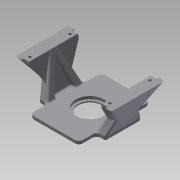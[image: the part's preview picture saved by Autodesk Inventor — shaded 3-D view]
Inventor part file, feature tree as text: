
AUTODESK INVENTOR PART (.ipt)
format: ipt  version: 2015 (Build 190159000, 159)  size: 1,136,128 bytes
history: native  units: in
note: dims shown in document units (in); Inventor stores cm internally (conversion verified against a paired STEP export)
features: fillet x9, sketch x8, extrude x6, plane x3, loft x3, mirror x1
ambient origin geometry x8: Origin, YZ Plane, XZ Plane, XY Plane, X Axis, Y Axis, Z Axis, Center Point
bodies: Solid1 (feature_tree)
feature tree (30):
  extrude  "Extrusion1"  Depth=3.1496in
  extrude  "Extrusion2"  Depth=0.3937in
  plane  "Work Plane1"
  plane  "Work Plane2"
  loft  "Loft3"
  loft  "Loft4"
  fillet  "Fillet1"  Radius=0.1181in
  fillet  "Fillet3"  Radius=1.4961in
  fillet  "Fillet4"  Radius=0.12in
  extrude  "Extrusion6"  Depth=2.126in
  extrude  "Extrusion7"  Depth=0.1772in
  fillet  "Fillet6"  Radius=0.2362in
  loft  "Loft5"
  fillet  "Fillet8"  Radius=0.2362in
  plane  "Work Plane3"
  extrude  "Extrusion8"  Depth=0.1181in
  fillet  "Fillet9"  Radius=2.1654in
  fillet  "Fillet10"  Radius=2.9528in
  fillet  "Fillet11"  Radius=1.5748in
  mirror  "Mirror3"
  fillet  "Fillet12"  Radius=3.2283in
  extrude  "Extrusion9"  Depth=0.1181in
  sketch  "Sketch3"  dims[d0=1.0433in d1=3.1496in]
  sketch  "Sketch11"  dims[d2=2.1654in d3=0.3937in d4=1.5748in]
  sketch  "Sketch12"  dims[d5=0.1772in d6=2.9528in]
  sketch  "Sketch13"  dims[d8=0.1673in d9=0.0in d10=1.2598in d11=0.1181in d12=0.0in d15=1.4961in d16=0.12in]
  sketch  "Sketch17"  dims[d19=1.6142in d20=2.126in]
  sketch  "Sketch18"  dims[d21=2.3622in d43=0.1772in d46=0.2362in]
  sketch  "Sketch19"  dims[d49=1.2598in d52=1.4764in d53=0.2362in]
  sketch  "Sketch20"  dims[d54=0.0in d55=90.0deg d56=0.0in d57=90.0deg d58=0.0394in d59=2.1654in d60=2.9528in d61=1.5748in d62=3.2283in d63=0.374in d64=0.4724in d65=0.0787in d66=0.0in d67=90.0deg d68=0.0in d69=90.0deg d70=0.0984in d72=0.0787in d74=0.0787in d75=0.0787in d76=0.0787in d77=0.0787in d80=0.3937in d81=0.0in d82=1.7717in d83=0.12in d84=0.3937in d85=0.0in d87=0.0787in d89=0.0787in d90=1.8701in d91=1.0827in d92=0.7874in d93=0.0in d94=0.0787in d95=0.9449in d96=0.1969in d97=0.3937in d98=2.1654in d99=0.0787in d102=0.0197in d103=0.0591in d104=0.0in d105=90.0deg d106=0.0in d107=90.0deg d108=0.0394in d109=0.0394in d110=0.0787in d111=0.0591in d112=1.2598in d113=0.1181in d114=0.0in]
